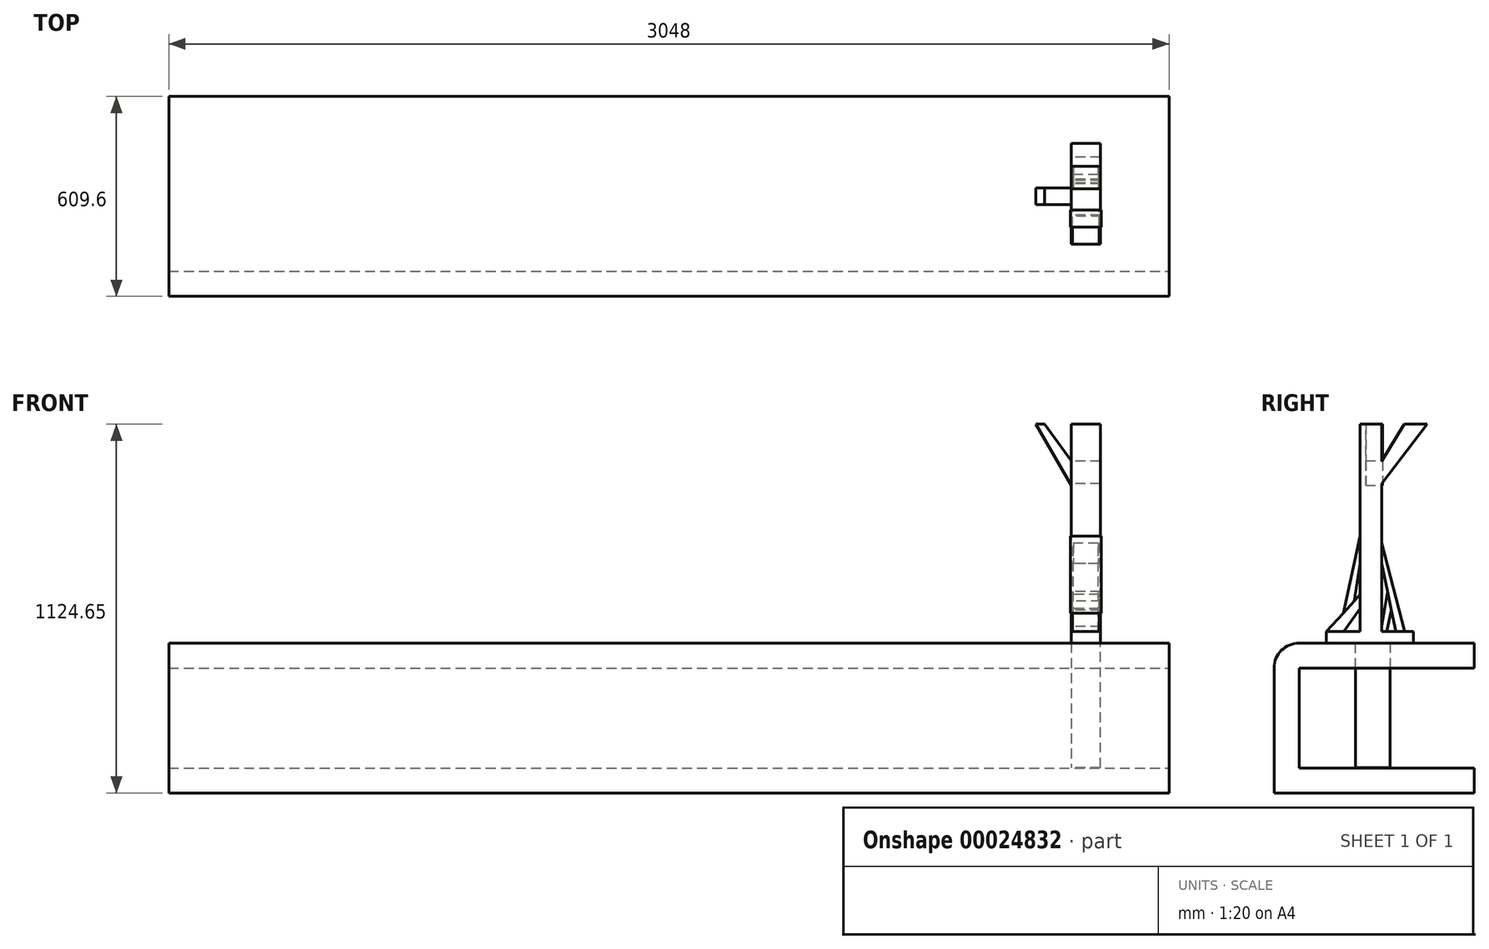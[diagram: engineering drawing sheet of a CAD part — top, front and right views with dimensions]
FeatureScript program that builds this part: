
annotation { "Feature Type Name" : "Feature", "Feature Type Description" : "" }
export const myFeature = defineFeature(function(context is Context, id is Id, definition is map)
    precondition{}
    {
        {
            var Q0;
            Q0=qCreatedBy(makeId("Top.planeOp"),FACE);
            var sketch = newSketch(context, id + "F0", { "sketchPlane" : qUnion([Q0])});
            skLineSegment(sketch, "E0.rect.bottom", {"start": v(-1524, 304.8) * mm, "end": v(1524, 304.8) * mm});
            skLineSegment(sketch, "E0.rect.top", {"start": v(-1524, -304.8) * mm, "end": v(1524, -304.8) * mm});
            skLineSegment(sketch, "E0.rect.left", {"start": v(-1524, 304.8) * mm, "end": v(-1524, -304.8) * mm});
            skLineSegment(sketch, "E0.rect.right", {"start": v(1524, 304.8) * mm, "end": v(1524, -304.8) * mm});
            skPoint(sketch, "E0.rect.middle", {"position": v(0, 0) * mm});
            skSolve(sketch);
        }
        {
            var Q0;
            Q0=makeQuery(id+"F0.imprint","IMPRINT",FACE,{"disambiguationData":[TD([[makeQuery(id+"F0.imprint","IMPRINT",EDGE,{"derivedFrom":sQuery(id+"F0.wireOp",EDGE,"E0.rect.bottom")}),-1.0]])]});
            extrude(context, id + "F1", {"entities" : qUnion([Q0]), "oppositeDirection" : true, "depth" : 457.2 * mm});
        }
        {
            var Q0;
            Q0=makeQuery(id+"F1.opExtrude","SWEPT_FACE",FACE,{"disambiguationData":[OSD([sQuery(id+"F0.wireOp",EDGE,"E0.rect.right")])]});
            var sketch = newSketch(context, id + "F2", { "sketchPlane" : qUnion([Q0])});
            skLineSegment(sketch, "E1.0", {"start": v(304.8, -457.2) * mm, "end": v(-304.8, -457.2) * mm});
            skLineSegment(sketch, "E1.1", {"start": v(304.8, -457.2) * mm, "end": v(304.8, 0) * mm});
            skLineSegment(sketch, "E1.2", {"start": v(304.8, 0) * mm, "end": v(-304.8, 0) * mm});
            skLineSegment(sketch, "E1.3", {"start": v(-304.8, -457.2) * mm, "end": v(-304.8, 0) * mm});
            skLineSegment(sketch, "E2.0", {"start": v(228.6, -381) * mm, "end": v(-228.6, -381) * mm});
            skLineSegment(sketch, "E2.1", {"start": v(228.6, -381) * mm, "end": v(228.6, -76.2) * mm});
            skLineSegment(sketch, "E2.2", {"start": v(228.6, -76.2) * mm, "end": v(-228.6, -76.2) * mm});
            skLineSegment(sketch, "E2.3", {"start": v(-228.6, -381) * mm, "end": v(-228.6, -76.2) * mm});
            skLineSegment(sketch, "E3", {"start": v(228.6, -381) * mm, "end": v(304.8, -381) * mm});
            skLineSegment(sketch, "E4", {"start": v(228.6, -76.2) * mm, "end": v(304.8, -76.2) * mm});
            skSolve(sketch);
        }
        {
            var Q0;
            Q0=makeQuery(id+"F2.imprint","IMPRINT",FACE,{"disambiguationData":[TD([[makeQuery(id+"F2.imprint","IMPRINT",EDGE,{"derivedFrom":sQuery(id+"F2.wireOp",EDGE,"E2.0")}),-1.0]])]});
            var Q1;
            Q1=makeQuery(id+"F2.imprint","IMPRINT",FACE,{"disambiguationData":[TD([[makeQuery(id+"F2.imprint","IMPRINT",EDGE,{"derivedFrom":sQuery(id+"F2.wireOp",EDGE,"E2.1")}),-1.0]])]});
            extrude(context, id + "F3", {"entities" : qUnion([Q0, Q1]), "operationType" : NewBodyOperationType.REMOVE, "endBound" : BoundingType.UP_TO_NEXT, "oppositeDirection" : true, "depth" : 25.4 * mm});
        }
        {
            var Q0;
            Q0=makeQuery(id+"F1.opExtrude","CAP_EDGE",EDGE,{"disambiguationData":[OSD([sQuery(id+"F0.wireOp",EDGE,"E0.rect.top")])],"isStart":true});
            fillet(context, id + "F4", {"entities" : qUnion([Q0]), "radius" : 76.2 * mm, "tangentPropagation" : true, "allowEdgeOverflow" : false});
        }
        {
            var Q0;
            Q0=qCreatedBy(makeId("Right.planeOp"),FACE);
            cPlane(context, id + "F5", {"entities" : qUnion([Q0]), "cplaneType" : CPlaneType.OFFSET, "offset" : 1270 * mm, "width" : 152.4 * mm, "height" : 152.4 * mm});
        }
        {
            var Q0;
            Q0=qCreatedBy(id+"F5.planeOp",FACE);
            var sketch = newSketch(context, id + "F6", { "sketchPlane" : qUnion([Q0])});
            skLineSegment(sketch, "E5", {"start": v(-56.38, -379.32) * mm, "end": v(-56.38, 0) * mm});
            skLineSegment(sketch, "E6", {"start": v(-56.38, 0) * mm, "end": v(-145.24, 0) * mm});
            skLineSegment(sketch, "E7", {"start": v(-145.24, 0) * mm, "end": v(-145.24, 34.77) * mm});
            skLineSegment(sketch, "E8", {"start": v(-145.24, 34.77) * mm, "end": v(119.56, 34.77) * mm});
            skLineSegment(sketch, "E9", {"start": v(119.56, 34.77) * mm, "end": v(119.56, 0) * mm});
            skLineSegment(sketch, "E10", {"start": v(119.56, 0) * mm, "end": v(48.53, 0) * mm});
            skLineSegment(sketch, "E11", {"start": v(48.53, 0) * mm, "end": v(48.53, -379.32) * mm});
            skLineSegment(sketch, "E12", {"start": v(48.53, -379.32) * mm, "end": v(-56.38, -379.32) * mm});
            skLineSegment(sketch, "E13", {"start": v(-42.17, 34.77) * mm, "end": v(-42.17, 667.45) * mm});
            skLineSegment(sketch, "E14", {"start": v(-42.17, 667.45) * mm, "end": v(23.59, 667.45) * mm});
            skLineSegment(sketch, "E15", {"start": v(23.59, 667.45) * mm, "end": v(23.59, 34.77) * mm});
            skLineSegment(sketch, "E16", {"start": v(-145.24, 34.77) * mm, "end": v(-42.17, 148.5) * mm});
            skLineSegment(sketch, "E17", {"start": v(-91.93, 34.77) * mm, "end": v(-42.17, 105.02) * mm});
            skLineSegment(sketch, "E18", {"start": v(66.24, 34.77) * mm, "end": v(23.59, 242.7) * mm});
            skLineSegment(sketch, "E19", {"start": v(92.9, 34.77) * mm, "end": v(23.59, 304.9) * mm});
            skLineSegment(sketch, "E20", {"start": v(-93.7, 91.64) * mm, "end": v(-42.17, 326.23) * mm});
            skLineSegment(sketch, "E21", {"start": v(-60.46, 128.32) * mm, "end": v(-42.17, 242.7) * mm});
            skLineSegment(sketch, "E22", {"start": v(38.66, 34.77) * mm, "end": v(52.73, 100.65) * mm});
            skLineSegment(sketch, "E23", {"start": v(23.59, 50.32) * mm, "end": v(41.19, 156.9) * mm});
            skLineSegment(sketch, "E24", {"start": v(23.59, 554.76) * mm, "end": v(92.23, 667.45) * mm});
            skLineSegment(sketch, "E25", {"start": v(92.23, 667.45) * mm, "end": v(161.2, 667.45) * mm});
            skLineSegment(sketch, "E26", {"start": v(161.2, 667.45) * mm, "end": v(23.59, 485.8) * mm});
            skSolve(sketch);
        }
        {
            var Q0;
            Q0=makeQuery(id+"F6.imprint","IMPRINT",FACE,{"disambiguationData":[TD([[makeQuery(id+"F6.imprint","IMPRINT",EDGE,{"derivedFrom":sQuery(id+"F6.wireOp",EDGE,"E5")}),-1.0]])]});
            var Q1;
            {var subQ6=sQuery(id+"F6.wireOp",EDGE,"E14");Q1=makeQuery(id+"F6.imprint","IMPRINT",FACE,{"disambiguationData":[TD([[makeQuery(id+"F6.imprint","IMPRINT",EDGE,{"derivedFrom":subQ6}),-1.0]])]});}
            var Q2;
            {var subQ1=sQuery(id+"F6.wireOp",EDGE,"E24");Q2=makeQuery(id+"F6.imprint","IMPRINT",FACE,{"disambiguationData":[TD([[makeQuery(id+"F6.imprint","IMPRINT",EDGE,{"derivedFrom":subQ1}),-1.0]])]});}
            extrude(context, id + "F7", {"entities" : qUnion([Q0, Q1, Q2]), "endBound" : BoundingType.SYMMETRIC, "depth" : 88.9 * mm});
        }
        {
            var Q0;
            {var subQ0=sQuery(id+"F6.wireOp",EDGE,"E19");Q0=makeQuery(id+"F6.imprint","IMPRINT",FACE,{"disambiguationData":[TD([[makeQuery(id+"F6.imprint","IMPRINT",EDGE,{"derivedFrom":subQ0}),1.0]])]});}
            extrude(context, id + "F8", {"entities" : qUnion([Q0]), "endBound" : BoundingType.SYMMETRIC, "depth" : 76.2 * mm});
        }
        {
            var Q0;
            {var subQ1=sQuery(id+"F6.wireOp",EDGE,"E22");Q0=makeQuery(id+"F6.imprint","IMPRINT",FACE,{"disambiguationData":[TD([[makeQuery(id+"F6.imprint","IMPRINT",EDGE,{"derivedFrom":subQ1}),1.0]])]});}
            extrude(context, id + "F9", {"entities" : qUnion([Q0]), "endBound" : BoundingType.SYMMETRIC, "depth" : 88.9 * mm});
        }
        {
            var Q0;
            {var subQ0=sQuery(id+"F6.wireOp",EDGE,"E17");Q0=makeQuery(id+"F6.imprint","IMPRINT",FACE,{"disambiguationData":[TD([[makeQuery(id+"F6.imprint","IMPRINT",EDGE,{"derivedFrom":subQ0}),1.0]])]});}
            extrude(context, id + "F10", {"entities" : qUnion([Q0]), "endBound" : BoundingType.SYMMETRIC, "depth" : 81.28 * mm});
        }
        {
            var Q0;
            {var subQ1=sQuery(id+"F6.wireOp",EDGE,"E20");Q0=makeQuery(id+"F6.imprint","IMPRINT",FACE,{"disambiguationData":[TD([[makeQuery(id+"F6.imprint","IMPRINT",EDGE,{"derivedFrom":subQ1}),-1.0]])]});}
            extrude(context, id + "F11", {"entities" : qUnion([Q0]), "endBound" : BoundingType.SYMMETRIC, "depth" : 93.98 * mm});
        }
        {
            var Q0;
            Q0=qCreatedBy(makeId("Front.planeOp"),FACE);
            var sketch = newSketch(context, id + "F12", { "sketchPlane" : qUnion([Q0])});
            skLineSegment(sketch, "E27.0", {"start": v(1314.45, 667.45) * mm, "end": v(1225.55, 667.45) * mm});
            skLineSegment(sketch, "E28", {"start": v(1501.4, 667.45) * mm, "end": v(1314.45, 403.8) * mm});
            skLineSegment(sketch, "E29", {"start": v(1501.4, 667.45) * mm, "end": v(1446.04, 667.45) * mm});
            skLineSegment(sketch, "E30", {"start": v(1446.04, 667.45) * mm, "end": v(1314.45, 481.86) * mm});
            skLineSegment(sketch, "E31", {"start": v(1314.45, 481.86) * mm, "end": v(1314.45, 403.8) * mm});
            skLineSegment(sketch, "E32", {"start": v(1144.78, 667.45) * mm, "end": v(1225.55, 556.2) * mm});
            skLineSegment(sketch, "E33", {"start": v(1225.55, 556.2) * mm, "end": v(1225.55, 480.95) * mm});
            skLineSegment(sketch, "E34", {"start": v(1225.55, 480.95) * mm, "end": v(1118.42, 667.45) * mm});
            skLineSegment(sketch, "E35", {"start": v(1118.42, 667.45) * mm, "end": v(1144.78, 667.45) * mm});
            skSolve(sketch);
        }
        {
            var Q0;
            Q0=makeQuery(id+"F12.imprint","IMPRINT",FACE,{"disambiguationData":[TD([[makeQuery(id+"F12.imprint","IMPRINT",EDGE,{"derivedFrom":sQuery(id+"F12.wireOp",EDGE,"E32")}),-1.0]])]});
            extrude(context, id + "F13", {"entities" : qUnion([Q0]), "operationType" : NewBodyOperationType.ADD, "endBound" : BoundingType.SYMMETRIC, "depth" : 50.8 * mm});
        }
    });
